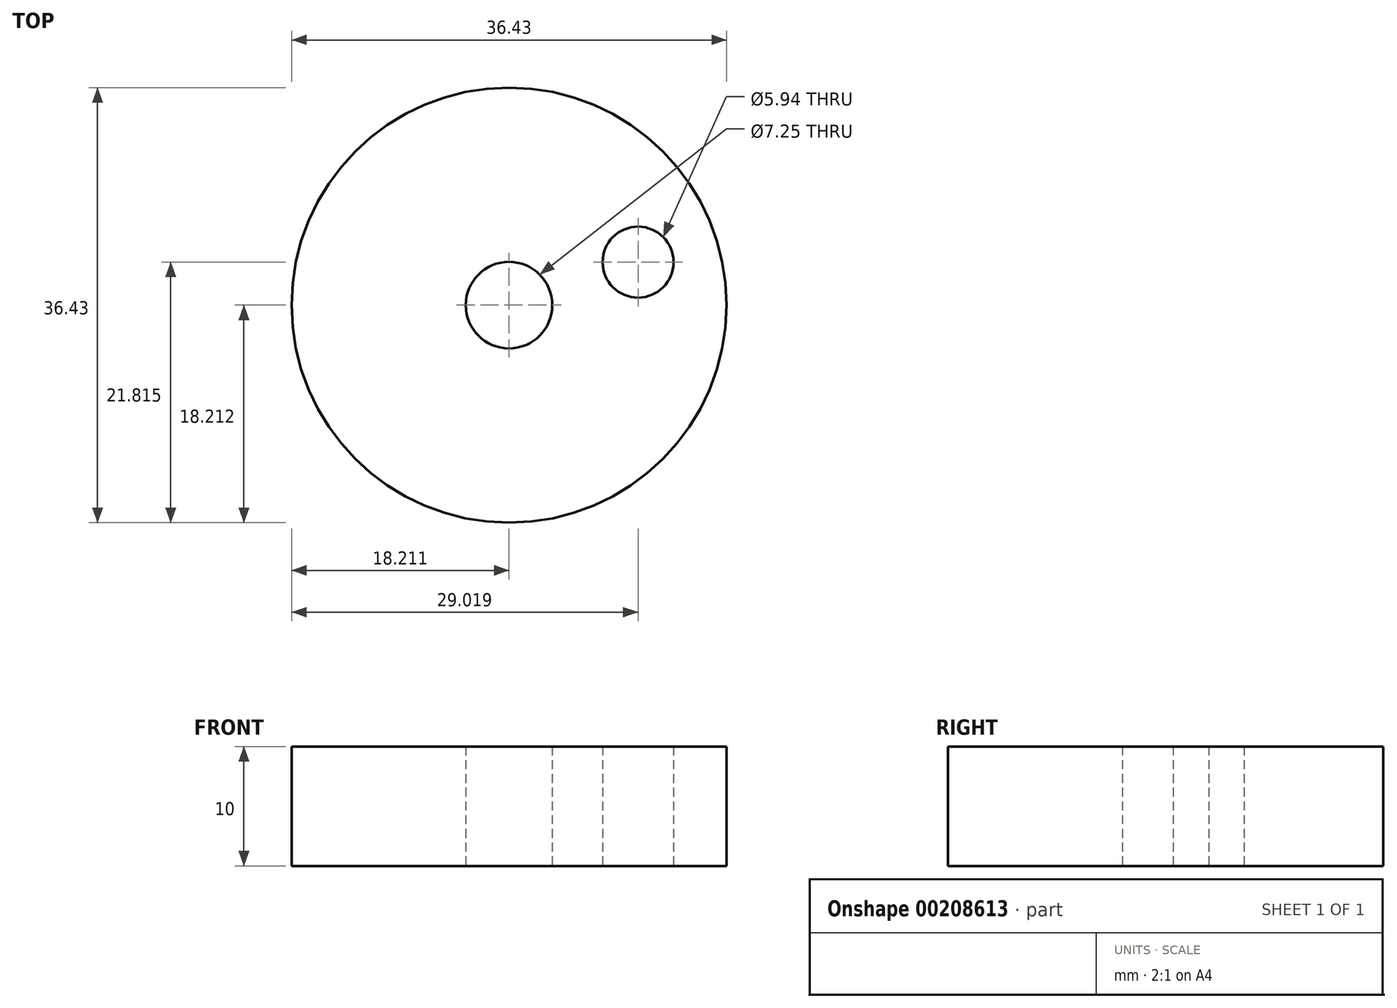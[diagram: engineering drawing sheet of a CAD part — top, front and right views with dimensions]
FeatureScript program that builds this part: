
annotation { "Feature Type Name" : "Feature", "Feature Type Description" : "" }
export const myFeature = defineFeature(function(context is Context, id is Id, definition is map)
    precondition{}
    {
        {
            var Q0;
            Q0=qCreatedBy(makeId("Top.planeOp"),FACE);
            var sketch = newSketch(context, id + "F0", { "sketchPlane" : qUnion([Q0])});
            skCircle(sketch, "E0", {"center": v(-65.67, -41.79) * mm, "radius": 18.21 * mm});
            skCircle(sketch, "E1", {"center": v(-54.86, -38.19) * mm, "radius": 2.97 * mm});
            skCircle(sketch, "E2", {"center": v(-65.67, -41.79) * mm, "radius": 3.62 * mm});
            skSolve(sketch);
        }
        {
            var Q0;
            Q0=makeQuery(id+"F0.imprint","IMPRINT",FACE,{"disambiguationData":[TD([[makeQuery(id+"F0.imprint","IMPRINT",EDGE,{"derivedFrom":sQuery(id+"F0.wireOp",EDGE,"E0")}),1.0]])]});
            extrude(context, id + "F1", {"entities" : qUnion([Q0]), "depth" : 10 * mm});
        }
    });
